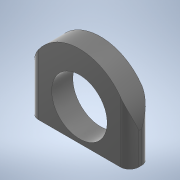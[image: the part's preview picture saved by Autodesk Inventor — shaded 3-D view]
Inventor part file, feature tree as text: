
AUTODESK INVENTOR PART (.ipt)
format: ipt  version: 2020 (Build 240168000, 168)  size: 184,832 bytes
history: native  units: mm
features: projected_geometry x9, sketch x5, extrude x4, other x1, fillet x1
ambient origin geometry x8: Origin, YZ Plane, XZ Plane, XY Plane, X Axis, Y Axis, Z Axis, Center Point
bodies: Body1 (feature_tree)
feature tree (20):
  other  "Твердое тело1"
  sketch  "Эскиз1"
  extrude  "Выдавливание1"  Depth=30.0mm
  fillet  "Сопряжение1"  Radius=3.0mm
  extrude  "Выдавливание2"  Depth=38.0mm
  extrude  "Выдавливание3"  Depth=8.0mm
  extrude  "Выдавливание4"  Depth=35.0mm TaperAngle=0.0deg
  sketch  "Эскиз2"
  sketch  "Эскиз3"
  projected_geometry  "Спроецированная петля1"
  projected_geometry  "Спроецированная петля2"
  projected_geometry  "Спроецированная петля3"
  projected_geometry  "Спроецированная петля4"
  projected_geometry  "Спроецированная петля5"
  projected_geometry  "Спроецированная петля6"
  sketch  "Эскиз4"
  projected_geometry  "Спроецированная петля7"
  projected_geometry  "Спроецированная петля8"
  projected_geometry  "Спроецированная петля9"
  sketch  "Эскиз5"
